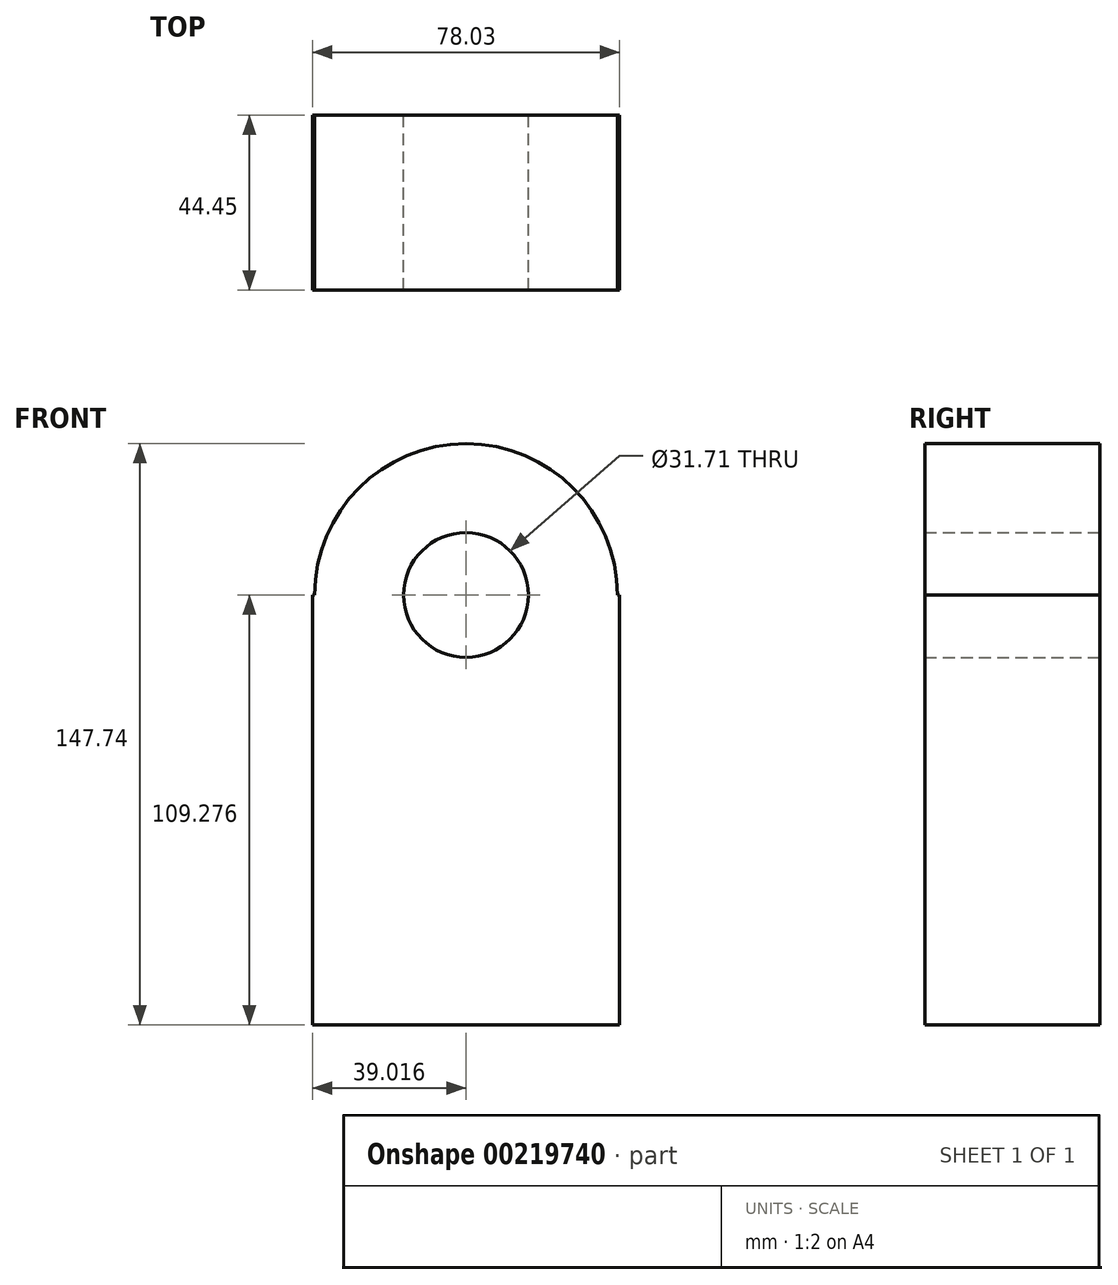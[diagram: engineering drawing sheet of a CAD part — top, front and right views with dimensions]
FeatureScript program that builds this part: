
annotation { "Feature Type Name" : "Feature", "Feature Type Description" : "" }
export const myFeature = defineFeature(function(context is Context, id is Id, definition is map)
    precondition{}
    {
        {
            var Q0;
            Q0=qCreatedBy(makeId("Front.planeOp"),FACE);
            var sketch = newSketch(context, id + "F0", { "sketchPlane" : qUnion([Q0])});
            skLineSegment(sketch, "E0.bottom", {"start": v(-44.59, 49.59) * mm, "end": v(-44.04, 49.59) * mm});
            skLineSegment(sketch, "E0.top", {"start": v(-44.59, -59.69) * mm, "end": v(33.44, -59.69) * mm});
            skLineSegment(sketch, "E0.left", {"start": v(-44.59, 49.59) * mm, "end": v(-44.59, -59.69) * mm});
            skLineSegment(sketch, "E0.right", {"start": v(33.44, 49.59) * mm, "end": v(33.44, -59.69) * mm});
            skArc(sketch, "E1", {"start": v(32.89, 49.59) * mm, "mid": v(-5.57, 88.05) * mm, "end": v(-44.04, 49.59) * mm});
            skCircle(sketch, "E2", {"center": v(-5.57, 49.59) * mm, "radius": 15.86 * mm});
            skLineSegment(sketch, "E3.trimOffspring", {"start": v(32.89, 49.59) * mm, "end": v(33.44, 49.59) * mm});
            skSolve(sketch);
        }
        {
            var Q0;
            Q0=makeQuery(id+"F0.imprint","IMPRINT",FACE,{"disambiguationData":[TD([[makeQuery(id+"F0.imprint","IMPRINT",EDGE,{"derivedFrom":sQuery(id+"F0.wireOp",EDGE,"E0.bottom")}),-1.0]])]});
            extrude(context, id + "F1", {"entities" : qUnion([Q0]), "depth" : 44.45 * mm});
        }
    });
